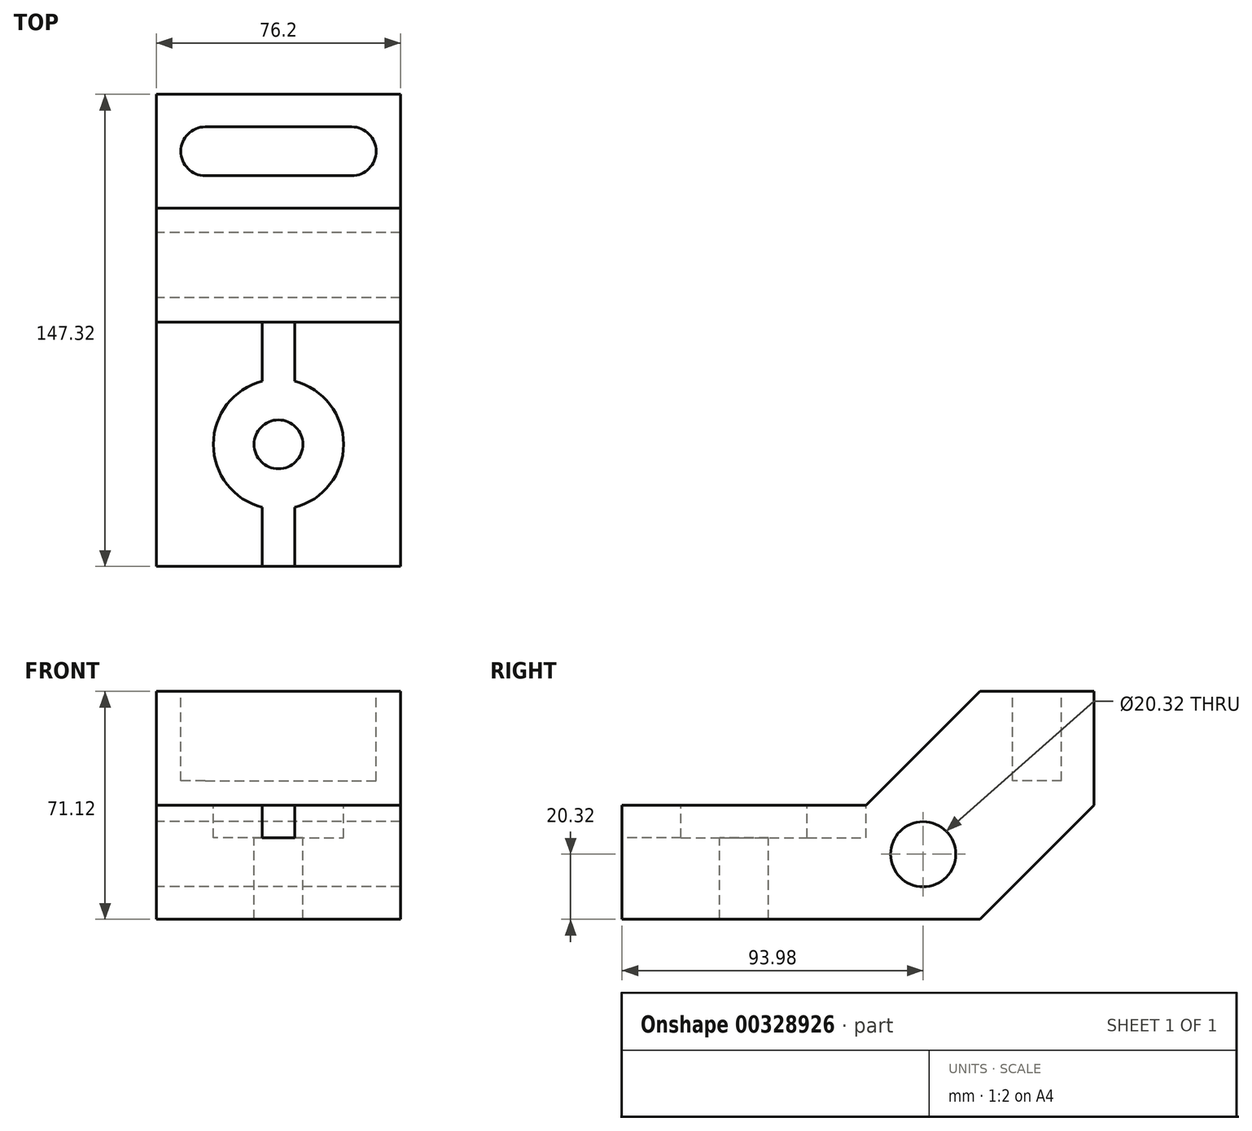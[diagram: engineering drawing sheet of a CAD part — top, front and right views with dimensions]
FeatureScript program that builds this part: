
annotation { "Feature Type Name" : "Feature", "Feature Type Description" : "" }
export const myFeature = defineFeature(function(context is Context, id is Id, definition is map)
    precondition{}
    {
        {
            var Q0;
            Q0=qCreatedBy(makeId("Right.planeOp"),FACE);
            var sketch = newSketch(context, id + "F0", { "sketchPlane" : qUnion([Q0])});
            skLineSegment(sketch, "E0", {"start": v(0, 0) * mm, "end": v(111.76, 0) * mm});
            skLineSegment(sketch, "E1", {"start": v(147.32, 35.56) * mm, "end": v(147.32, 71.12) * mm});
            skLineSegment(sketch, "E2", {"start": v(147.32, 71.12) * mm, "end": v(111.76, 71.12) * mm});
            skLineSegment(sketch, "E3", {"start": v(0, 0) * mm, "end": v(0, 35.56) * mm});
            skLineSegment(sketch, "E4", {"start": v(0, 35.56) * mm, "end": v(76.2, 35.56) * mm});
            skLineSegment(sketch, "E5", {"start": v(76.2, 35.56) * mm, "end": v(111.76, 71.12) * mm});
            skLineSegment(sketch, "E6", {"start": v(111.76, 0) * mm, "end": v(147.32, 35.56) * mm});
            skPoint(sketch, "E7.orphan", {"position": v(147.32, 0) * mm});
            skLineSegment(sketch, "E8", {"start": v(0, 0) * mm, "end": v(147.32, 0) * mm, "construction": true});
            skLineSegment(sketch, "E9", {"start": v(147.32, 0) * mm, "end": v(147.32, 71.12) * mm, "construction": true});
            skCircle(sketch, "E10", {"center": v(93.98, 20.32) * mm, "radius": 10.16 * mm});
            skSolve(sketch);
        }
        {
            var Q0;
            Q0=makeQuery(id+"F0.imprint","IMPRINT",FACE,{"disambiguationData":[TD([[makeQuery(id+"F0.imprint","IMPRINT",EDGE,{"derivedFrom":sQuery(id+"F0.wireOp",EDGE,"E0")}),1.0]])]});
            extrude(context, id + "F1", {"entities" : qUnion([Q0]), "depth" : 76.2 * mm});
        }
        {
            var Q0;
            Q0=makeQuery(id+"F1.opExtrude","SWEPT_FACE",FACE,{"disambiguationData":[OSD([sQuery(id+"F0.wireOp",EDGE,"E4")])]});
            var sketch = newSketch(context, id + "F2", { "sketchPlane" : qUnion([Q0])});
            skCircle(sketch, "E11", {"center": v(38.1, 38.1) * mm, "radius": 7.62 * mm});
            skLineSegment(sketch, "E12", {"start": v(38.1, 0) * mm, "end": v(43.18, 0) * mm});
            skLineSegment(sketch, "E13", {"start": v(43.18, 0) * mm, "end": v(43.18, 76.2) * mm});
            skLineSegment(sketch, "E14", {"start": v(43.18, 76.2) * mm, "end": v(33.02, 76.2) * mm});
            skLineSegment(sketch, "E15", {"start": v(33.02, 76.2) * mm, "end": v(33.02, 0) * mm});
            skLineSegment(sketch, "E16", {"start": v(33.02, 0) * mm, "end": v(38.1, 0) * mm});
            skCircle(sketch, "E17", {"center": v(38.1, 38.1) * mm, "radius": 20.32 * mm});
            skSolve(sketch);
        }
        {
            var Q0;
            {var subQ2=sQuery(id+"F2.wireOp",EDGE,"E12");Q0=makeQuery(id+"F2.imprint","IMPRINT",FACE,{"disambiguationData":[TD([[makeQuery(id+"F2.imprint","IMPRINT",EDGE,{"derivedFrom":subQ2}),-1.0]])]});}
            var Q1;
            {var subQ0=sQuery(id+"F2.wireOp",EDGE,"E14");Q1=makeQuery(id+"F2.imprint","IMPRINT",FACE,{"disambiguationData":[TD([[makeQuery(id+"F2.imprint","IMPRINT",EDGE,{"derivedFrom":subQ0}),1.0]])]});}
            extrude(context, id + "F3", {"entities" : qUnion([Q0, Q1]), "operationType" : NewBodyOperationType.REMOVE, "oppositeDirection" : true, "depth" : 10.16 * mm});
        }
        {
            var Q0;
            Q0=sQuery(id+"F2.wireOp",VERTEX,"E11.center");
            var Q1;
            Q1=makeQuery(id+"F1.opExtrude","SWEPT_BODY",BODY,{"disambiguationData":[OSD([sQuery(id+"F0.wireOp",EDGE,"E0"),sQuery(id+"F0.wireOp",EDGE,"E1"),sQuery(id+"F0.wireOp",EDGE,"E2"),sQuery(id+"F0.wireOp",EDGE,"E3"),sQuery(id+"F0.wireOp",EDGE,"E4"),sQuery(id+"F0.wireOp",EDGE,"E5"),sQuery(id+"F0.wireOp",EDGE,"E6"),sQuery(id+"F0.wireOp",EDGE,"E10")])]});
            hole(context, id + "F4", {"style" : HoleStyle.C_BORE, "endStyle" : HoleEndStyle.THROUGH, "holeDiameter" : 15.24 * mm, "cBoreDiameter" : 40.64 * mm, "cBoreDepth" : 10.16 * mm, "tappedDepth" : 12.7 * mm, "tapClearance" : 3, "locations" : qUnion([Q0]), "scope" : qUnion([Q1])});
        }
        {
            var Q0;
            Q0=makeQuery(id+"F1.opExtrude","SWEPT_FACE",FACE,{"disambiguationData":[OSD([sQuery(id+"F0.wireOp",EDGE,"E2")])]});
            var sketch = newSketch(context, id + "F5", { "sketchPlane" : qUnion([Q0])});
            skLineSegment(sketch, "E18", {"start": v(15.24, 137.16) * mm, "end": v(60.96, 137.16) * mm});
            skLineSegment(sketch, "E19", {"start": v(15.24, 121.92) * mm, "end": v(60.96, 121.92) * mm});
            skArc(sketch, "E20", {"start": v(15.24, 121.92) * mm, "mid": v(7.62, 129.54) * mm, "end": v(15.24, 137.16) * mm});
            skArc(sketch, "E21", {"start": v(60.96, 137.16) * mm, "mid": v(68.58, 129.54) * mm, "end": v(60.96, 121.92) * mm});
            skSolve(sketch);
        }
        {
            var Q0;
            Q0=makeQuery(id+"F5.imprint","IMPRINT",FACE,{"disambiguationData":[TD([[makeQuery(id+"F5.imprint","IMPRINT",EDGE,{"derivedFrom":sQuery(id+"F5.wireOp",EDGE,"E18")}),-1.0]])]});
            extrude(context, id + "F6", {"entities" : qUnion([Q0]), "operationType" : NewBodyOperationType.REMOVE, "oppositeDirection" : true, "depth" : 27.94 * mm});
        }
    });
